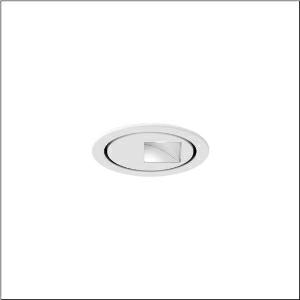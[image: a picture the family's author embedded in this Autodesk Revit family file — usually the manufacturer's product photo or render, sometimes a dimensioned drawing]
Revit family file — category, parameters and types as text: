
# Revit family: lunis_11_micro_round_51dj11cd1wn21
name_source: partatom
category: Lighting Fixtures
units: mm (PartAtom-declared; Revit-internal decimal feet)

## family parameters
Cut with Voids When Loaded = No
Host = Face
Light Source = No
Part Type = Normal
Room Calculation Point = No
Round Connector Dimension = Use Diameter
Shared = No

## types (1)
- Lunis 11 micro round (1 x LED 4000K / CRI = 90 (unbekannt), 1210 lm, 4000K)
    Apparent Load = 20 VA
    CIE Flux Codes = 42 75 96 100 100
    Color Rendering = 90
    Color Temperature = 4000K
    Default Elevation = 1800 mm
    Description = Lunis 11 micro round, downlight, light control with wallwasher, of highly reflective aluminium, highly specular, light emission: direct distribution, LED rated luminous flux: 1.210lm, light colour: 940, with terminal, 5-pole, mains connection: 220..230V, AC, 50/60Hz, LED module, of aluminium, highly specular, white, diameter: 114mm, clamping range: 1..40mm, recessing ring, of plastic, traffic white (RAL 9016), protection rating (complete): IP20, insulation class (complete): insulation class II (safety insulation), certification: CE, permissible ambient temperature for indoor applications: 0..+35°C, packaging unit: 1 piece
    Height = 0 mm  [stored 0 ft]
    Lamp = 1 x LED 4000K / CRI >= 90 (unbekannt)
    Lamp Light Flux = 1210 lm
    Lamp count = 1
    Length = 114 mm
    Luminous efficacy = 61 lm/W
    Manufacturer = Siteco
    ModVariant = No
    Model = 51DJ11CD1WN21
    Mounting Place = Ceiling
    Mounting Type = Recessed
    Number of Poles = 1
    OnlyDefault = Yes
    Power Factor = 1
    Product Name = Lunis 11 micro round
    Product group = downlight
    ProductGroupID = 400
    Protection Class = Protection class II
    Protection Degree = IP 20
    RLX_Detail_Level = 1
    RLX_Emergency_Light_Flux = 0 lm
    RLX_Emergency_Type = 0
    RLX_Emergency_Type_DB = No
    RlxData = <blob elided: 41093 chars, md5=94841d98>
    Socket = socket
    Standby Power = 0 W
    System Light Flux = 1210 lm
    System Power = 20 W
    Type Comments = Product without accessories
    Type Image = l_1004773.jpg
    URL = http://relux.com
    VarID = ---
    Voltage = 0 V
    Weight = 0.00 kg
    Width = 114 mm

note: [stored X ft] marks values corroborated as IEEE doubles in the binary element streams (Revit-internal decimal feet)

## geometry (parser evidence)
native form markers: Blend x4, Sweep x10
no freeform markers — native parametric forms only
